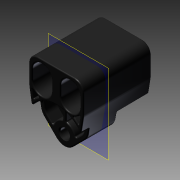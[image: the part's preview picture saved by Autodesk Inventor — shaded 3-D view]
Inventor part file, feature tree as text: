
AUTODESK INVENTOR PART (.ipt)
format: ipt  version: 2013 (Build 170138000, 138)  size: 2,391,040 bytes
history: native  units: mm (DEFAULTED — no unit token found)
features: imported_body x1, plane x1
ambient origin geometry x8: Origin, YZ Plane, XZ Plane, XY Plane, X Axis, Y Axis, Z Axis, Center Point
bodies: Solid1 (feature_tree)
feature tree (2):
  imported_body  "Base1"
  plane  "Work Plane1"
